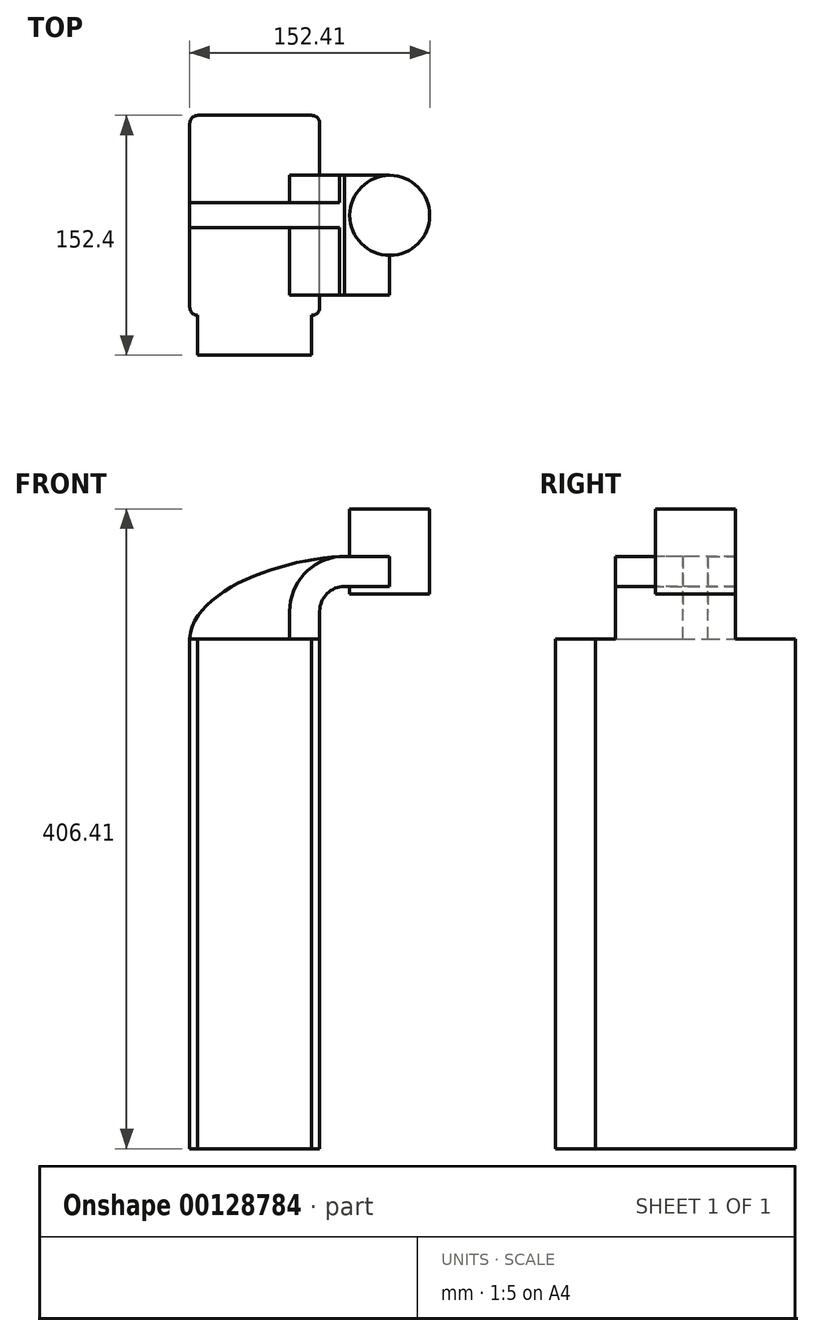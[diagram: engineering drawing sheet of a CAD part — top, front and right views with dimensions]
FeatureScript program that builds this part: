
annotation { "Feature Type Name" : "Feature", "Feature Type Description" : "" }
export const myFeature = defineFeature(function(context is Context, id is Id, definition is map)
    precondition{}
    {
        {
            var Q0;
            Q0=qCreatedBy(makeId("Front.planeOp"),FACE);
            var sketch = newSketch(context, id + "F0", { "sketchPlane" : qUnion([Q0])});
            skLineSegment(sketch, "E0.rect.bottom", {"start": v(-41.28, 9.52) * mm, "end": v(41.28, 9.52) * mm});
            skLineSegment(sketch, "E0.rect.top", {"start": v(-41.28, -9.52) * mm, "end": v(41.28, -9.52) * mm});
            skLineSegment(sketch, "E0.rect.left", {"start": v(-41.28, 9.52) * mm, "end": v(-41.28, -9.52) * mm});
            skLineSegment(sketch, "E0.rect.right", {"start": v(41.28, 9.52) * mm, "end": v(41.28, -9.52) * mm});
            skPoint(sketch, "E0.rect.middle", {"position": v(0, 0) * mm});
            skLineSegment(sketch, "E1", {"start": v(41.28, 9.52) * mm, "end": v(41.28, 27) * mm});
            skArc(sketch, "E2", {"start": v(41.28, 27) * mm, "mid": v(45.92, 38.23) * mm, "end": v(57.15, 42.88) * mm});
            skLineSegment(sketch, "E3", {"start": v(57.15, 42.88) * mm, "end": v(85.72, 42.88) * mm});
            skLineSegment(sketch, "E4.rect.bottom", {"start": v(60.32, 38.1) * mm, "end": v(111.12, 38.1) * mm});
            skLineSegment(sketch, "E4.rect.top", {"start": v(60.32, 66.68) * mm, "end": v(111.12, 66.68) * mm});
            skLineSegment(sketch, "E4.rect.left", {"start": v(60.32, 38.1) * mm, "end": v(60.32, 66.68) * mm});
            skLineSegment(sketch, "E4.rect.right", {"start": v(111.13, 38.1) * mm, "end": v(111.12, 66.68) * mm});
            skPoint(sketch, "E4.rect.middle", {"position": v(85.72, 52.39) * mm});
            skLineSegment(sketch, "E5.0", {"start": v(57.15, 61.93) * mm, "end": v(85.72, 61.93) * mm});
            skArc(sketch, "E5.1", {"start": v(22.23, 27) * mm, "mid": v(32.45, 51.7) * mm, "end": v(57.15, 61.93) * mm});
            skLineSegment(sketch, "E5.2", {"start": v(22.23, 9.52) * mm, "end": v(22.23, 27) * mm});
            skLineSegment(sketch, "E6", {"start": v(85.72, 38.1) * mm, "end": v(85.72, 66.68) * mm});
            skFitSpline(sketch, "E7", {"points": [v(-41.28, 9.53) * mm, v(57.15, 61.93) * mm], "startDerivative": vector(5.2, 92.34) * mm, "endDerivative": vector(120.92, 4.22) * mm});
            skSolve(sketch);
        }
        {
            var Q0;
            Q0=makeQuery(id+"F0.imprint","IMPRINT",FACE,{"disambiguationData":[TD([[makeQuery(id+"F0.imprint","IMPRINT",EDGE,{"derivedFrom":sQuery(id+"F0.wireOp",EDGE,"E0.rect.top")}),1.0]])]});
            extrude(context, id + "F1", {"entities" : qUnion([Q0]), "endBound" : BoundingType.SYMMETRIC, "depth" : 127 * mm});
        }
        {
            var Q0;
            {var subQ9=sQuery(id+"F0.wireOp",EDGE,"E1");Q0=makeQuery(id+"F0.imprint","IMPRINT",FACE,{"disambiguationData":[TD([[makeQuery(id+"F0.imprint","IMPRINT",EDGE,{"derivedFrom":subQ9}),1.0]])]});}
            var Q1;
            {var subQ0=sQuery(id+"F0.wireOp",EDGE,"E6");var subQ1=sQuery(id+"F0.wireOp",EDGE,"E3");var subQ2=makeQuery(id+"F0.imprint","INTERSECT",VERTEX,{"derivedFrom":[subQ1,subQ0]});Q1=makeQuery(id+"F0.imprint","IMPRINT",FACE,{"disambiguationData":[TD([[makeQuery(id+"F0.imprint","IMPRINT",EDGE,{"disambiguationData":[TD([[subQ2,1.0]])],"derivedFrom":subQ1}),1.0]])]});}
            extrude(context, id + "F2", {"entities" : qUnion([Q0, Q1]), "operationType" : NewBodyOperationType.ADD, "endBound" : BoundingType.SYMMETRIC, "depth" : 50.8 * mm});
        }
        {
            var Q0;
            {var subQ3=sQuery(id+"F0.wireOp",EDGE,"E5.2");Q0=makeQuery(id+"F0.imprint","IMPRINT",FACE,{"disambiguationData":[TD([[makeQuery(id+"F0.imprint","IMPRINT",EDGE,{"derivedFrom":subQ3}),1.0]])]});}
            extrude(context, id + "F3", {"entities" : qUnion([Q0]), "operationType" : NewBodyOperationType.ADD, "endBound" : BoundingType.SYMMETRIC, "depth" : 15.88 * mm});
        }
        {
            var Q0;
            {var subQ5=sQuery(id+"F0.wireOp",EDGE,"E4.rect.right");Q0=makeQuery(id+"F0.imprint","IMPRINT",FACE,{"disambiguationData":[TD([[makeQuery(id+"F0.imprint","IMPRINT",EDGE,{"derivedFrom":subQ5}),1.0]])]});}
            var Q1;
            Q1=sQuery(id+"F0.wireOp",EDGE,"E6");
            revolve(context, id + "F4", {"operationType" : NewBodyOperationType.ADD, "entities" : qUnion([Q0]), "axis" : qUnion([Q1]), "revolveType" : RevolveType.FULL});
        }
        {
            var Q0;
            Q0=makeQuery(id+"F1.opExtrude","CAP_EDGE",EDGE,{"disambiguationData":[OSD([sQuery(id+"F0.wireOp",EDGE,"E0.rect.right")])],"isStart":false});
            var Q1;
            Q1=makeQuery(id+"F1.opExtrude","CAP_EDGE",EDGE,{"disambiguationData":[OSD([sQuery(id+"F0.wireOp",EDGE,"E0.rect.left")])],"isStart":false});
            var Q2;
            Q2=makeQuery(id+"F1.opExtrude","CAP_EDGE",EDGE,{"disambiguationData":[OSD([sQuery(id+"F0.wireOp",EDGE,"E0.rect.right")])],"isStart":true});
            var Q3;
            Q3=makeQuery(id+"F1.opExtrude","CAP_EDGE",EDGE,{"disambiguationData":[OSD([sQuery(id+"F0.wireOp",EDGE,"E0.rect.left")])],"isStart":true});
            fillet(context, id + "F5", {"entities" : qUnion([Q0, Q1, Q2, Q3]), "radius" : 5.08 * mm, "tangentPropagation" : true, "allowEdgeOverflow" : false});
        }
        {
            var Q0;
            Q0=makeQuery(id+"F4.opRevolve","SWEPT_FACE",FACE,{"disambiguationData":[OSD([sQuery(id+"F0.wireOp",EDGE,"E4.rect.top")])]});
            extrude(context, id + "F6", {"entities" : qUnion([Q0]), "operationType" : NewBodyOperationType.ADD, "depth" : 25.4 * mm});
        }
        {
            var Q0;
            Q0=makeQuery(id+"F2.opExtrude","CAP_FACE",FACE,{"disambiguationData":[OSD([sQuery(id+"F0.wireOp",EDGE,"E0.rect.bottom"),sQuery(id+"F0.wireOp",EDGE,"E1"),sQuery(id+"F0.wireOp",EDGE,"E2"),sQuery(id+"F0.wireOp",EDGE,"E3"),sQuery(id+"F0.wireOp",EDGE,"E5.0"),sQuery(id+"F0.wireOp",EDGE,"E5.1"),sQuery(id+"F0.wireOp",EDGE,"E5.2"),sQuery(id+"F0.wireOp",EDGE,"E6"),sQuery(id+"F0.wireOp",EDGE,"E7")])],"isStart":false});
            var Q1;
            Q1=makeQuery(id+"F1.opExtrude","CAP_FACE",FACE,{"disambiguationData":[OSD([sQuery(id+"F0.wireOp",EDGE,"E0.rect.bottom"),sQuery(id+"F0.wireOp",EDGE,"E0.rect.top"),sQuery(id+"F0.wireOp",EDGE,"E0.rect.left"),sQuery(id+"F0.wireOp",EDGE,"E0.rect.right")])],"isStart":false});
            extrude(context, id + "F7", {"entities" : qUnion([Q0, Q1]), "operationType" : NewBodyOperationType.ADD, "depth" : 25.4 * mm});
        }
        {
            var Q0;
            {var subQ0=sQuery(id+"F0.wireOp",EDGE,"E0.rect.top");Q0=makeQuery(id+"F7.boolean.opBoolean","MERGE",FACE,{"derivedFrom":[makeQuery(id+"F1.opExtrude","SWEPT_FACE",FACE,{"disambiguationData":[OSD([subQ0])]}),makeQuery(id+"F7.opExtrude","SWEPT_FACE",FACE,{"disambiguationData":[OSD([subQ0])]})]});}
            extrude(context, id + "F8", {"entities" : qUnion([Q0]), "operationType" : NewBodyOperationType.ADD, "depth" : 304.8 * mm});
        }
    });
